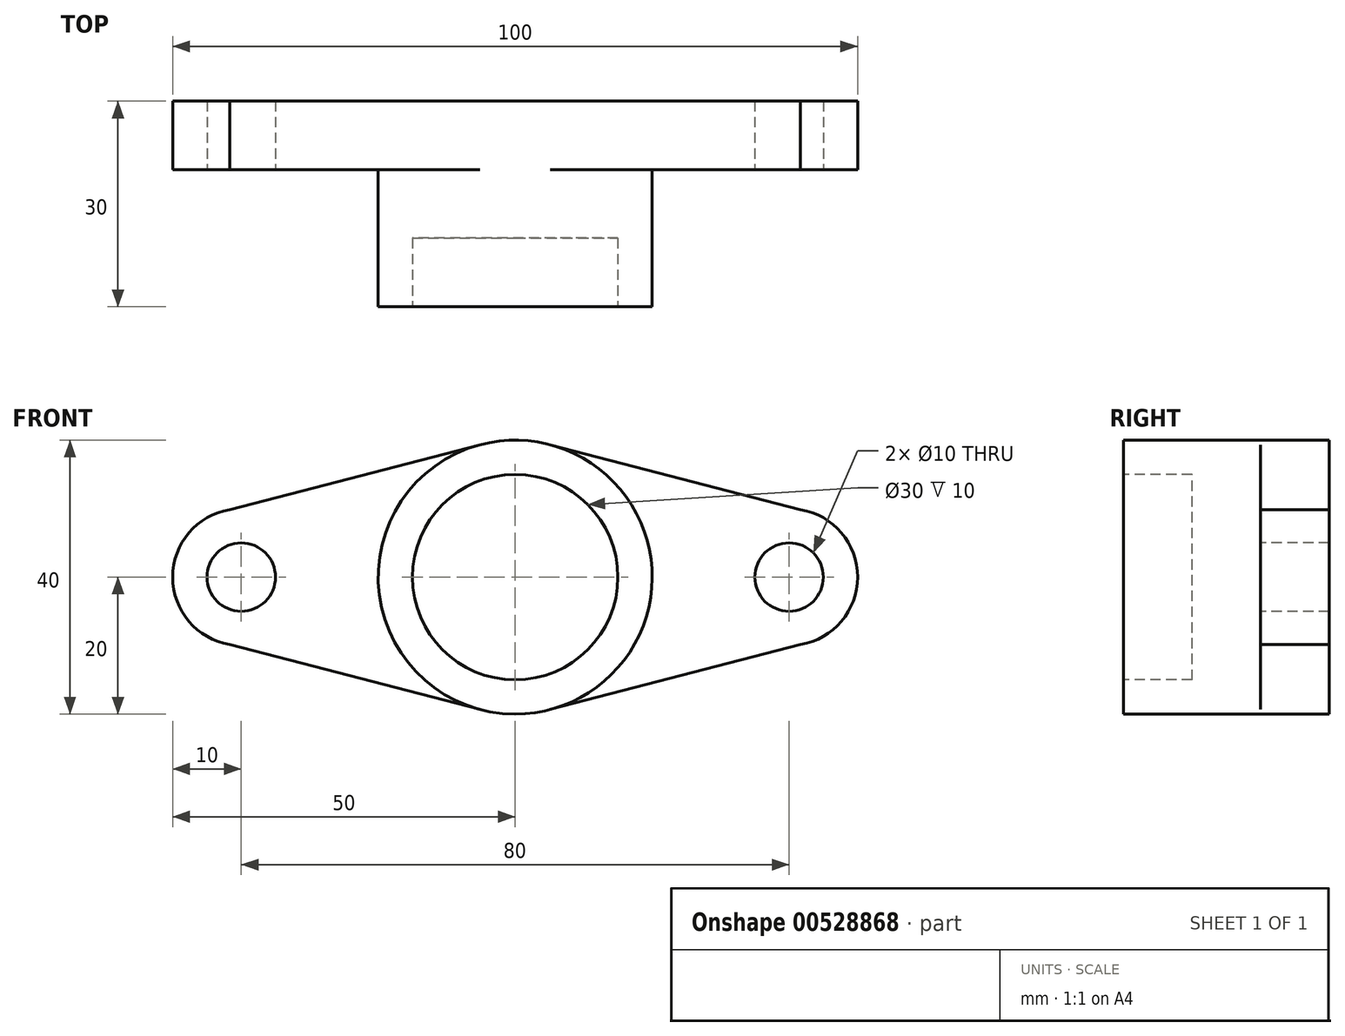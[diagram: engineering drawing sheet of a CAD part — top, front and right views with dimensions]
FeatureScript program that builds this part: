
annotation { "Feature Type Name" : "Feature", "Feature Type Description" : "" }
export const myFeature = defineFeature(function(context is Context, id is Id, definition is map)
    precondition{}
    {
        {
            var Q0;
            Q0=qCreatedBy(makeId("Front.planeOp"),FACE);
            var sketch = newSketch(context, id + "F0", { "sketchPlane" : qUnion([Q0])});
            skLineSegment(sketch, "E0", {"start": v(-40, 0) * mm, "end": v(40, 0) * mm, "construction": true});
            skLineSegment(sketch, "E1", {"start": v(0, 28.48) * mm, "end": v(0, -31.98) * mm, "construction": true});
            skArc(sketch, "E2", {"start": v(41.66, -9.86) * mm, "mid": v(50, 0) * mm, "end": v(41.66, 9.86) * mm});
            skArc(sketch, "E3.MirrorC", {"start": v(-41.66, -9.86) * mm, "mid": v(-50, 0) * mm, "end": v(-41.66, 9.86) * mm});
            skCircle(sketch, "E4", {"center": v(0, 0) * mm, "radius": 20 * mm});
            skLineSegment(sketch, "E5", {"start": v(41.66, -9.86) * mm, "end": v(5.16, -19.32) * mm});
            skLineSegment(sketch, "E6.MirrorCS", {"start": v(-41.66, -9.86) * mm, "end": v(-5.16, -19.32) * mm});
            skLineSegment(sketch, "E7.MirrorCS", {"start": v(41.66, 9.86) * mm, "end": v(5.16, 19.32) * mm});
            skLineSegment(sketch, "E8.MirrorCS", {"start": v(-41.66, 9.86) * mm, "end": v(-5.16, 19.32) * mm});
            skSolve(sketch);
        }
        {
            var Q0;
            Q0 = qSketchRegion(id + "F0", true);
            extrude(context, id + "F1", {"entities" : qUnion([Q0]), "depth" : 10 * mm, "offsetDistance" : 25 * mm});
        }
        {
            var Q0;
            Q0=makeQuery(id+"F1.opExtrude","CAP_FACE",FACE,{"disambiguationData":[OSD([sQuery(id+"F0.wireOp",EDGE,"E2"),sQuery(id+"F0.wireOp",EDGE,"E3.MirrorC"),sQuery(id+"F0.wireOp",EDGE,"E4"),sQuery(id+"F0.wireOp",EDGE,"E5"),sQuery(id+"F0.wireOp",EDGE,"E6.MirrorCS"),sQuery(id+"F0.wireOp",EDGE,"E7.MirrorCS"),sQuery(id+"F0.wireOp",EDGE,"E8.MirrorCS")])],"isStart":false});
            var sketch = newSketch(context, id + "F2", { "sketchPlane" : qUnion([Q0])});
            skLineSegment(sketch, "E9", {"start": v(0, 0) * mm, "end": v(40, 0) * mm, "construction": true});
            skPoint(sketch, "E9.endSnap0", {"position": v(50, 0) * mm});
            skCircle(sketch, "E10", {"center": v(40, 0) * mm, "radius": 5 * mm});
            skLineSegment(sketch, "E11", {"start": v(0, 24.3) * mm, "end": v(0, -31.12) * mm, "construction": true});
            skCircle(sketch, "E12.MirrorC", {"center": v(-40, 0) * mm, "radius": 5 * mm});
            skSolve(sketch);
        }
        {
            var Q0;
            Q0 = qSketchRegion(id + "F2", true);
            extrude(context, id + "F3", {"entities" : qUnion([Q0]), "operationType" : NewBodyOperationType.REMOVE, "endBound" : BoundingType.THROUGH_ALL, "oppositeDirection" : true, "depth" : 25 * mm, "offsetDistance" : 25 * mm});
        }
        {
            var Q0;
            Q0=makeQuery(id+"F1.opExtrude","CAP_FACE",FACE,{"disambiguationData":[OSD([sQuery(id+"F0.wireOp",EDGE,"E2"),sQuery(id+"F0.wireOp",EDGE,"E3.MirrorC"),sQuery(id+"F0.wireOp",EDGE,"E4"),sQuery(id+"F0.wireOp",EDGE,"E5"),sQuery(id+"F0.wireOp",EDGE,"E6.MirrorCS"),sQuery(id+"F0.wireOp",EDGE,"E7.MirrorCS"),sQuery(id+"F0.wireOp",EDGE,"E8.MirrorCS")])],"isStart":false});
            var sketch = newSketch(context, id + "F4", { "sketchPlane" : qUnion([Q0])});
            skCircle(sketch, "E13", {"center": v(0, 0) * mm, "radius": 20 * mm});
            skSolve(sketch);
        }
        {
            var Q0;
            {var subQ0=sQuery(id+"F4.wireOp",EDGE,"E13");var subQ1=makeQuery(id+"F4.imprint","INTERSECT",VERTEX,{"derivedFrom":[makeQuery(id+"F1.opExtrude","CAP_EDGE",EDGE,{"disambiguationData":[OSD([sQuery(id+"F0.wireOp",EDGE,"E7.MirrorCS")])],"isStart":false}),subQ0]});Q0=makeQuery(id+"F4.imprint","IMPRINT",FACE,{"disambiguationData":[TD([[makeQuery(id+"F4.imprint","IMPRINT",EDGE,{"disambiguationData":[TD([[subQ1,-1.0]])],"derivedFrom":subQ0}),1.0]])]});}
            extrude(context, id + "F5", {"entities" : qUnion([Q0]), "operationType" : NewBodyOperationType.ADD, "depth" : 20 * mm, "offsetDistance" : 25 * mm});
        }
        {
            var Q0;
            Q0=makeQuery(id+"F5.opExtrude","CAP_FACE",FACE,{"disambiguationData":[OSD([sQuery(id+"F4.wireOp",EDGE,"E13")])],"isStart":false});
            var sketch = newSketch(context, id + "F6", { "sketchPlane" : qUnion([Q0])});
            skCircle(sketch, "E14", {"center": v(0, 0) * mm, "radius": 15 * mm});
            skSolve(sketch);
        }
        {
            var Q0;
            Q0=makeQuery(id+"F6.imprint","IMPRINT",FACE,{"disambiguationData":[TD([[makeQuery(id+"F6.imprint","IMPRINT",EDGE,{"derivedFrom":sQuery(id+"F6.wireOp",EDGE,"E14")}),1.0]])]});
            extrude(context, id + "F7", {"entities" : qUnion([Q0]), "operationType" : NewBodyOperationType.REMOVE, "oppositeDirection" : true, "depth" : 10 * mm, "offsetDistance" : 25 * mm});
        }
    });
